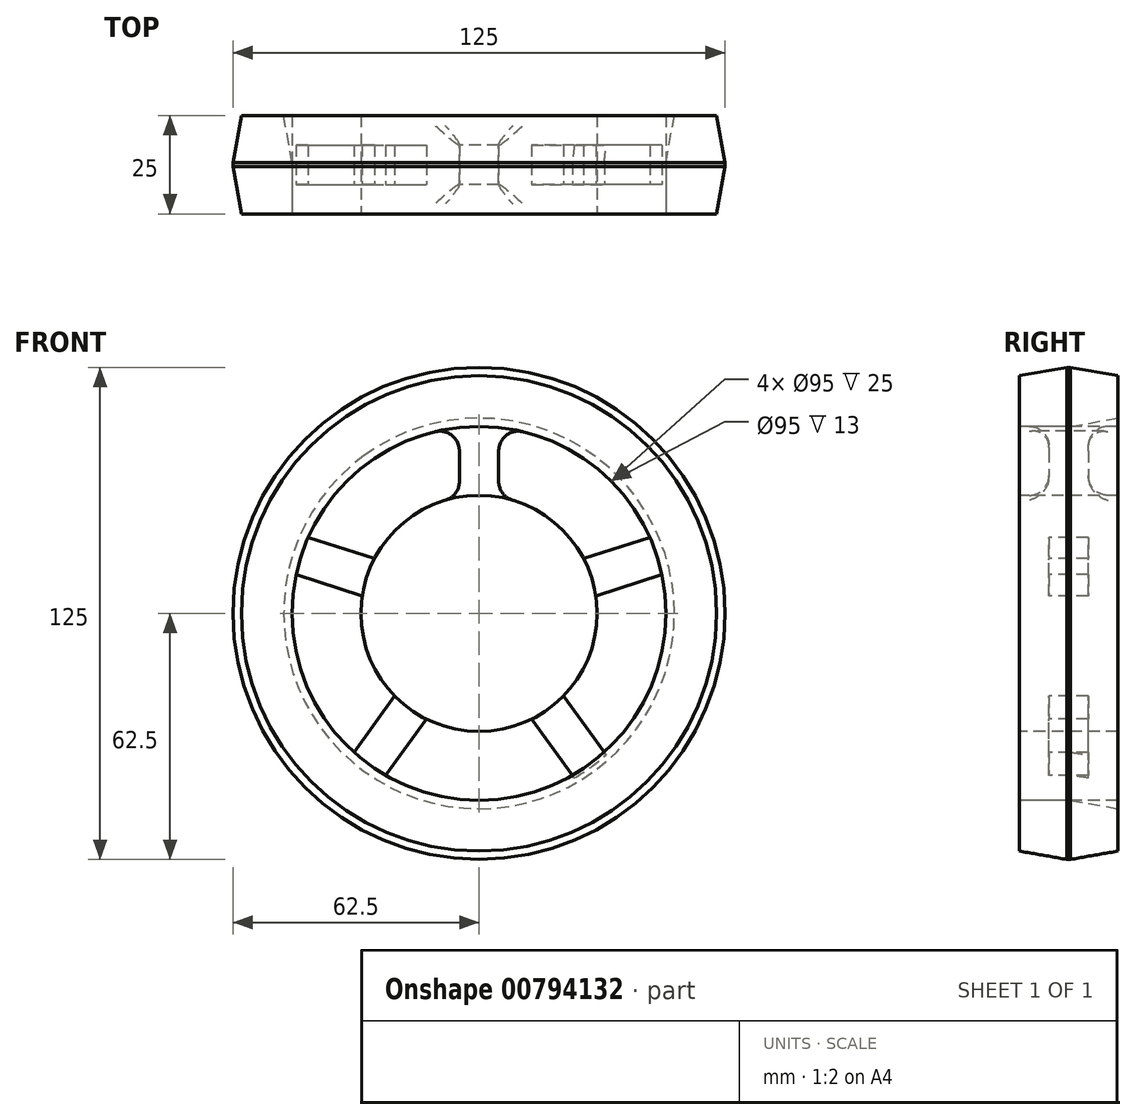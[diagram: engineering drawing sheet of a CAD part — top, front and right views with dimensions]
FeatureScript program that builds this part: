
annotation { "Feature Type Name" : "Feature", "Feature Type Description" : "" }
export const myFeature = defineFeature(function(context is Context, id is Id, definition is map)
    precondition{}
    {
        {
            var Q0;
            Q0=qCreatedBy(makeId("Front.planeOp"),FACE);
            var sketch = newSketch(context, id + "F0", { "sketchPlane" : qUnion([Q0])});
            skCircle(sketch, "E0", {"center": v(0, 0) * mm, "radius": 62.5 * mm});
            skSolve(sketch);
        }
        {
            var Q0;
            Q0 = qSketchRegion(id + "F0", true);
            extrude(context, id + "F1", {"entities" : qUnion([Q0]), "endBound" : BoundingType.SYMMETRIC, "depth" : 25 * mm, "offsetDistance" : 25 * mm});
        }
        {
            var Q0;
            Q0=makeQuery(id+"F1.opExtrude","CAP_FACE",FACE,{"disambiguationData":[OSD([sQuery(id+"F0.wireOp",EDGE,"E0")])],"isStart":false});
            var sketch = newSketch(context, id + "F2", { "sketchPlane" : qUnion([Q0])});
            skCircle(sketch, "E1", {"center": v(0, 0) * mm, "radius": 30 * mm});
            skCircle(sketch, "E2", {"center": v(0, 0) * mm, "radius": 47.5 * mm});
            skSolve(sketch);
        }
        {
            var Q0;
            Q0=makeQuery(id+"F2.imprint","IMPRINT",FACE,{"disambiguationData":[TD([[makeQuery(id+"F2.imprint","IMPRINT",EDGE,{"derivedFrom":sQuery(id+"F2.wireOp",EDGE,"E1")}),-1.0]])]});
            var Q1;
            Q1 = qSketchRegion(id + "F2", true);
            extrude(context, id + "F3", {"entities" : qUnion([Q0, Q1]), "operationType" : NewBodyOperationType.REMOVE, "oppositeDirection" : true, "depth" : 25 * mm, "offsetDistance" : 25 * mm});
        }
        {
            var Q0;
            Q0=qCreatedBy(makeId("Front.planeOp"),FACE);
            var sketch = newSketch(context, id + "F4", { "sketchPlane" : qUnion([Q0])});
            skLineSegment(sketch, "E3.bottom", {"start": v(-5, 57.26) * mm, "end": v(5, 57.26) * mm});
            skLineSegment(sketch, "E3.top", {"start": v(-5, 22.26) * mm, "end": v(5, 22.26) * mm});
            skLineSegment(sketch, "E3.left", {"start": v(-5, 57.26) * mm, "end": v(-5, 22.26) * mm});
            skLineSegment(sketch, "E3.right", {"start": v(5, 57.26) * mm, "end": v(5, 22.26) * mm});
            skPoint(sketch, "E4", {"position": v(0, 57.26) * mm});
            skPoint(sketch, "E5", {"position": v(0, 0) * mm});
            skSolve(sketch);
        }
        {
            var Q0;
            Q0=makeQuery(id+"F4.imprint","IMPRINT",FACE,{"disambiguationData":[TD([[makeQuery(id+"F4.imprint","IMPRINT",EDGE,{"derivedFrom":sQuery(id+"F4.wireOp",EDGE,"E3.bottom")}),-1.0]])]});
            extrude(context, id + "F5", {"entities" : qUnion([Q0]), "operationType" : NewBodyOperationType.ADD, "endBound" : BoundingType.SYMMETRIC, "depth" : 10 * mm, "offsetDistance" : 25 * mm});
        }
        {
            var Q0;
            Q0=makeQuery(id+"F3.boolean.opBoolean","SPLIT",BODY,{"disambiguationData":[OD(0.0)],"derivedFrom":makeQuery(id+"F1.opExtrude","SWEPT_BODY",BODY,{"disambiguationData":[OSD([sQuery(id+"F0.wireOp",EDGE,"E0")])]})});
            var Q1;
            Q1=makeQuery(id+"F3.boolean.opBoolean","COPY",EDGE,{"derivedFrom":makeQuery(id+"F3.opExtrude","CAP_EDGE",EDGE,{"disambiguationData":[OSD([sQuery(id+"F2.wireOp",EDGE,"E1")])],"isStart":true})});
            circularPattern(context, id + "F6", {"entities" : qUnion([Q0]), "axis" : qUnion([Q1]), "angle" : 360 * degree, "instanceCount" : 5, "equalSpace" : true});
        }
        {
            var Q0;
            Q0=makeQuery(id+"F6.opPattern","COPY",EDGE,{"derivedFrom":makeQuery(id+"F1.opExtrude","CAP_EDGE",EDGE,{"disambiguationData":[OSD([sQuery(id+"F0.wireOp",EDGE,"E0")])],"isStart":false}),"instanceName":"4"});
            var Q1;
            Q1=makeQuery(id+"F1.opExtrude","CAP_EDGE",EDGE,{"disambiguationData":[OSD([sQuery(id+"F0.wireOp",EDGE,"E0")])],"isStart":false});
            var Q2;
            Q2=makeQuery(id+"F6.opPattern","COPY",EDGE,{"derivedFrom":makeQuery(id+"F1.opExtrude","CAP_EDGE",EDGE,{"disambiguationData":[OSD([sQuery(id+"F0.wireOp",EDGE,"E0")])],"isStart":false}),"instanceName":"2"});
            var Q3;
            Q3=makeQuery(id+"F6.opPattern","COPY",EDGE,{"derivedFrom":makeQuery(id+"F1.opExtrude","CAP_EDGE",EDGE,{"disambiguationData":[OSD([sQuery(id+"F0.wireOp",EDGE,"E0")])],"isStart":false}),"instanceName":"3"});
            var Q4;
            Q4=makeQuery(id+"F6.opPattern","COPY",EDGE,{"derivedFrom":makeQuery(id+"F1.opExtrude","CAP_EDGE",EDGE,{"disambiguationData":[OSD([sQuery(id+"F0.wireOp",EDGE,"E0")])],"isStart":false}),"instanceName":"1"});
            chamfer(context, id + "F7", {"entities" : qUnion([Q0, Q1, Q2, Q3, Q4]), "chamferType" : ChamferType.OFFSET_ANGLE, "width" : 12 * mm, "oppositeDirection" : true, "angle" : 10 * degree, "tangentPropagation" : true});
        }
        {
            var Q0;
            Q0=makeQuery(id+"F6.opPattern","COPY",EDGE,{"derivedFrom":makeQuery(id+"F1.opExtrude","CAP_EDGE",EDGE,{"disambiguationData":[OSD([sQuery(id+"F0.wireOp",EDGE,"E0")])],"isStart":true}),"instanceName":"4"});
            var Q1;
            Q1=makeQuery(id+"F6.opPattern","COPY",EDGE,{"derivedFrom":makeQuery(id+"F1.opExtrude","CAP_EDGE",EDGE,{"disambiguationData":[OSD([sQuery(id+"F0.wireOp",EDGE,"E0")])],"isStart":true}),"instanceName":"1"});
            var Q2;
            Q2=makeQuery(id+"F6.opPattern","COPY",EDGE,{"derivedFrom":makeQuery(id+"F1.opExtrude","CAP_EDGE",EDGE,{"disambiguationData":[OSD([sQuery(id+"F0.wireOp",EDGE,"E0")])],"isStart":true}),"instanceName":"2"});
            var Q3;
            {var subQ0=sQuery(id+"F0.wireOp",EDGE,"E0");Q3=makeQuery(id+"F6.opPattern","COPY",FACE,{"derivedFrom":makeQuery(id+"F3.boolean.opBoolean","SPLIT",FACE,{"disambiguationData":[TD([makeQuery(id+"F1.opExtrude","SWEPT_FACE",FACE,{"disambiguationData":[OSD([subQ0])]})])],"derivedFrom":makeQuery(id+"F1.opExtrude","CAP_FACE",FACE,{"disambiguationData":[OSD([subQ0])],"isStart":true})}),"instanceName":"3"});}
            var Q4;
            Q4=makeQuery(id+"F1.opExtrude","CAP_EDGE",EDGE,{"disambiguationData":[OSD([sQuery(id+"F0.wireOp",EDGE,"E0")])],"isStart":true});
            chamfer(context, id + "F8", {"entities" : qUnion([Q0, Q1, Q2, Q3, Q4]), "chamferType" : ChamferType.OFFSET_ANGLE, "width" : 12 * mm, "oppositeDirection" : false, "angle" : 10 * degree, "tangentPropagation" : true});
        }
        {
            var Q0;
            Q0=makeQuery(id+"F5.boolean.opBoolean","INTERSECT",EDGE,{"derivedFrom":[makeQuery(id+"F3.boolean.opBoolean","COPY",FACE,{"derivedFrom":makeQuery(id+"F3.opExtrude","SWEPT_FACE",FACE,{"disambiguationData":[OSD([sQuery(id+"F2.wireOp",EDGE,"E2")])]})}),makeQuery(id+"F5.opExtrude","CAP_FACE",FACE,{"disambiguationData":[OSD([sQuery(id+"F4.wireOp",EDGE,"E3.bottom"),sQuery(id+"F4.wireOp",EDGE,"E3.top"),sQuery(id+"F4.wireOp",EDGE,"E3.left"),sQuery(id+"F4.wireOp",EDGE,"E3.right")])],"isStart":false})]});
            var Q1;
            Q1=makeQuery(id+"F5.boolean.opBoolean","INTERSECT",EDGE,{"derivedFrom":[makeQuery(id+"F3.boolean.opBoolean","COPY",FACE,{"derivedFrom":makeQuery(id+"F3.opExtrude","SWEPT_FACE",FACE,{"disambiguationData":[OSD([sQuery(id+"F2.wireOp",EDGE,"E2")])]})}),makeQuery(id+"F5.opExtrude","SWEPT_FACE",FACE,{"disambiguationData":[OSD([sQuery(id+"F4.wireOp",EDGE,"E3.right")])]})]});
            var Q2;
            Q2=makeQuery(id+"F5.boolean.opBoolean","INTERSECT",EDGE,{"derivedFrom":[makeQuery(id+"F3.boolean.opBoolean","COPY",FACE,{"derivedFrom":makeQuery(id+"F3.opExtrude","SWEPT_FACE",FACE,{"disambiguationData":[OSD([sQuery(id+"F2.wireOp",EDGE,"E2")])]})}),makeQuery(id+"F5.opExtrude","SWEPT_FACE",FACE,{"disambiguationData":[OSD([sQuery(id+"F4.wireOp",EDGE,"E3.left")])]})]});
            var Q3;
            Q3=makeQuery(id+"F5.boolean.opBoolean","INTERSECT",EDGE,{"derivedFrom":[makeQuery(id+"F3.boolean.opBoolean","COPY",FACE,{"derivedFrom":makeQuery(id+"F3.opExtrude","SWEPT_FACE",FACE,{"disambiguationData":[OSD([sQuery(id+"F2.wireOp",EDGE,"E2")])]})}),makeQuery(id+"F5.opExtrude","CAP_FACE",FACE,{"disambiguationData":[OSD([sQuery(id+"F4.wireOp",EDGE,"E3.bottom"),sQuery(id+"F4.wireOp",EDGE,"E3.top"),sQuery(id+"F4.wireOp",EDGE,"E3.left"),sQuery(id+"F4.wireOp",EDGE,"E3.right")])],"isStart":true})]});
            var Q4;
            Q4=makeQuery(id+"F5.boolean.opBoolean","INTERSECT",EDGE,{"derivedFrom":[makeQuery(id+"F3.boolean.opBoolean","COPY",FACE,{"derivedFrom":makeQuery(id+"F3.opExtrude","SWEPT_FACE",FACE,{"disambiguationData":[OSD([sQuery(id+"F2.wireOp",EDGE,"E1")])]})}),makeQuery(id+"F5.opExtrude","CAP_FACE",FACE,{"disambiguationData":[OSD([sQuery(id+"F4.wireOp",EDGE,"E3.bottom"),sQuery(id+"F4.wireOp",EDGE,"E3.top"),sQuery(id+"F4.wireOp",EDGE,"E3.left"),sQuery(id+"F4.wireOp",EDGE,"E3.right")])],"isStart":true})]});
            var Q5;
            Q5=makeQuery(id+"F5.boolean.opBoolean","INTERSECT",EDGE,{"derivedFrom":[makeQuery(id+"F3.boolean.opBoolean","COPY",FACE,{"derivedFrom":makeQuery(id+"F3.opExtrude","SWEPT_FACE",FACE,{"disambiguationData":[OSD([sQuery(id+"F2.wireOp",EDGE,"E1")])]})}),makeQuery(id+"F5.opExtrude","SWEPT_FACE",FACE,{"disambiguationData":[OSD([sQuery(id+"F4.wireOp",EDGE,"E3.left")])]})]});
            var Q6;
            Q6=makeQuery(id+"F5.boolean.opBoolean","INTERSECT",EDGE,{"derivedFrom":[makeQuery(id+"F3.boolean.opBoolean","COPY",FACE,{"derivedFrom":makeQuery(id+"F3.opExtrude","SWEPT_FACE",FACE,{"disambiguationData":[OSD([sQuery(id+"F2.wireOp",EDGE,"E1")])]})}),makeQuery(id+"F5.opExtrude","SWEPT_FACE",FACE,{"disambiguationData":[OSD([sQuery(id+"F4.wireOp",EDGE,"E3.right")])]})]});
            var Q7;
            Q7=makeQuery(id+"F5.boolean.opBoolean","INTERSECT",EDGE,{"derivedFrom":[makeQuery(id+"F3.boolean.opBoolean","COPY",FACE,{"derivedFrom":makeQuery(id+"F3.opExtrude","SWEPT_FACE",FACE,{"disambiguationData":[OSD([sQuery(id+"F2.wireOp",EDGE,"E1")])]})}),makeQuery(id+"F5.opExtrude","CAP_FACE",FACE,{"disambiguationData":[OSD([sQuery(id+"F4.wireOp",EDGE,"E3.bottom"),sQuery(id+"F4.wireOp",EDGE,"E3.top"),sQuery(id+"F4.wireOp",EDGE,"E3.left"),sQuery(id+"F4.wireOp",EDGE,"E3.right")])],"isStart":false})]});
            fillet(context, id + "F9", {"entities" : qUnion([Q0, Q1, Q2, Q3, Q4, Q5, Q6, Q7]), "radius" : 5 * mm, "tangentPropagation" : true, "allowEdgeOverflow" : false});
        }
    });
